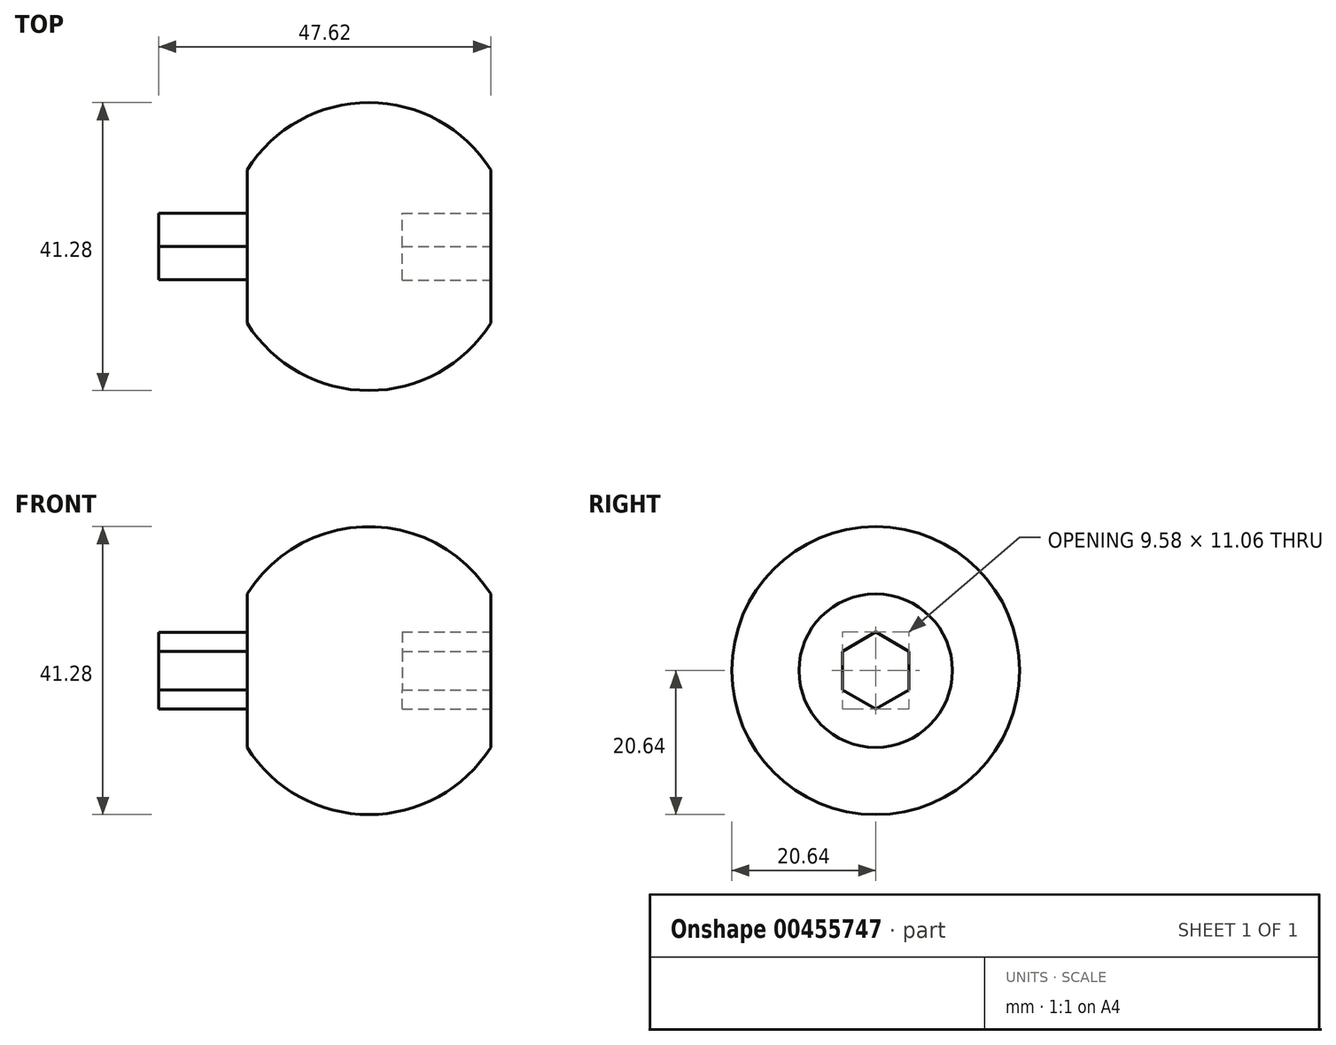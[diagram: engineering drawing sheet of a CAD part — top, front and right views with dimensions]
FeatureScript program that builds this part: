
annotation { "Feature Type Name" : "Feature", "Feature Type Description" : "" }
export const myFeature = defineFeature(function(context is Context, id is Id, definition is map)
    precondition{}
    {
        {
            var Q0;
            Q0=qCreatedBy(makeId("Front.planeOp"),FACE);
            var sketch = newSketch(context, id + "F0", { "sketchPlane" : qUnion([Q0])});
            skArc(sketch, "E0", {"start": v(17.46, 11) * mm, "mid": v(0, 20.64) * mm, "end": v(-17.46, 11) * mm});
            skLineSegment(sketch, "E1", {"start": v(-36.81, 0) * mm, "end": v(33.84, 0) * mm, "construction": true});
            skLineSegment(sketch, "E2", {"start": v(17.46, 0) * mm, "end": v(17.46, 11) * mm});
            skLineSegment(sketch, "E3", {"start": v(-17.46, 11) * mm, "end": v(-17.46, 0) * mm});
            skLineSegment(sketch, "E4", {"start": v(-17.46, 0) * mm, "end": v(17.46, 0) * mm});
            skSolve(sketch);
        }
        {
            var Q0;
            Q0 = qSketchRegion(id + "F0", true);
            var Q1;
            Q1=sQuery(id+"F0.wireOp",EDGE,"E1");
            revolve(context, id + "F1", {"entities" : qUnion([Q0]), "axis" : qUnion([Q1]), "revolveType" : RevolveType.FULL});
        }
        {
            var Q0;
            Q0=makeQuery(id+"F1.opRevolve","SWEPT_FACE",FACE,{"disambiguationData":[OSD([sQuery(id+"F0.wireOp",EDGE,"E2")])]});
            var sketch = newSketch(context, id + "F2", { "sketchPlane" : qUnion([Q0])});
            skCircle(sketch, "E5.cCircle", {"center": v(0, 0) * mm, "radius": 4.79 * mm, "construction": true});
            skLineSegment(sketch, "E5.0", {"start": v(4.79, 2.76) * mm, "end": v(4.79, -2.76) * mm});
            skLineSegment(sketch, "E5.1", {"start": v(4.79, -2.76) * mm, "end": v(0, -5.53) * mm});
            skLineSegment(sketch, "E5.2", {"start": v(0, -5.53) * mm, "end": v(-4.79, -2.76) * mm});
            skLineSegment(sketch, "E5.3", {"start": v(-4.79, -2.76) * mm, "end": v(-4.79, 2.76) * mm});
            skLineSegment(sketch, "E5.4", {"start": v(-4.79, 2.76) * mm, "end": v(0, 5.53) * mm});
            skLineSegment(sketch, "E5.5", {"start": v(0, 5.53) * mm, "end": v(4.79, 2.76) * mm});
            skPoint(sketch, "E5.0.midPoint", {"position": v(4.79, 0) * mm});
            skSolve(sketch);
        }
        {
            var Q0;
            Q0 = qSketchRegion(id + "F2", true);
            extrude(context, id + "F3", {"entities" : qUnion([Q0]), "operationType" : NewBodyOperationType.REMOVE, "oppositeDirection" : true, "depth" : 12.7 * mm, "offsetDistance" : 25.4 * mm});
        }
        {
            var Q0;
            Q0=makeQuery(id+"F1.opRevolve","SWEPT_FACE",FACE,{"disambiguationData":[OSD([sQuery(id+"F0.wireOp",EDGE,"E3")])]});
            var sketch = newSketch(context, id + "F4", { "sketchPlane" : qUnion([Q0])});
            skCircle(sketch, "E6.cCircle", {"center": v(0, 0) * mm, "radius": 4.76 * mm, "construction": true});
            skLineSegment(sketch, "E6.0", {"start": v(4.76, 2.75) * mm, "end": v(4.76, -2.75) * mm});
            skLineSegment(sketch, "E6.1", {"start": v(4.76, -2.75) * mm, "end": v(0, -5.5) * mm});
            skLineSegment(sketch, "E6.2", {"start": v(0, -5.5) * mm, "end": v(-4.76, -2.75) * mm});
            skLineSegment(sketch, "E6.3", {"start": v(-4.76, -2.75) * mm, "end": v(-4.76, 2.75) * mm});
            skLineSegment(sketch, "E6.4", {"start": v(-4.76, 2.75) * mm, "end": v(0, 5.5) * mm});
            skLineSegment(sketch, "E6.5", {"start": v(0, 5.5) * mm, "end": v(4.76, 2.75) * mm});
            skPoint(sketch, "E6.0.midPoint", {"position": v(4.76, 0) * mm});
            skSolve(sketch);
        }
        {
            var Q0;
            Q0 = qSketchRegion(id + "F4", true);
            extrude(context, id + "F5", {"entities" : qUnion([Q0]), "operationType" : NewBodyOperationType.ADD, "depth" : 12.7 * mm, "offsetDistance" : 25.4 * mm});
        }
    });
